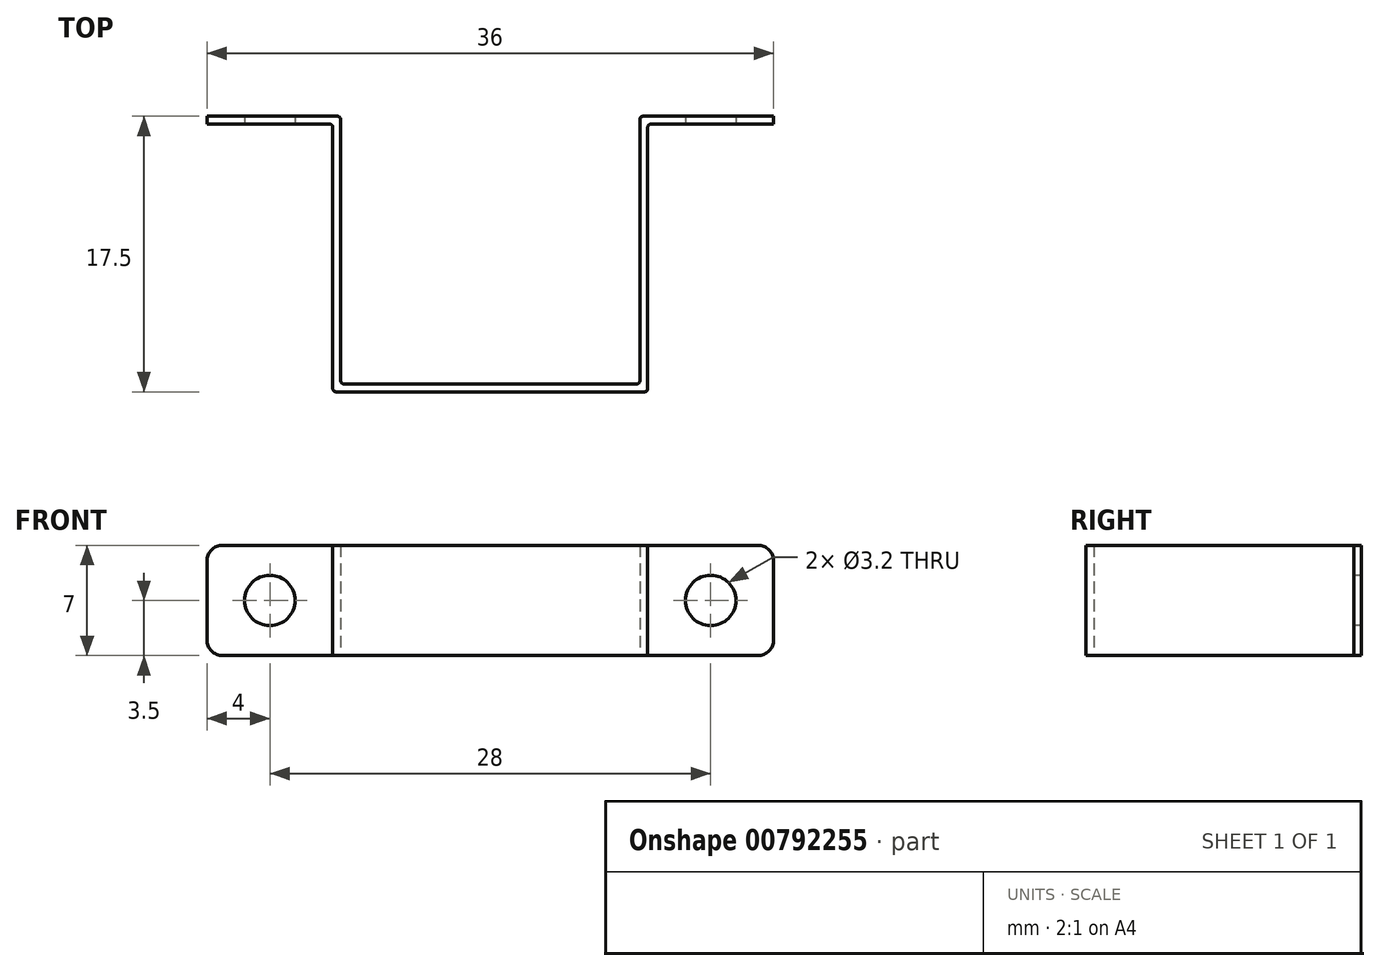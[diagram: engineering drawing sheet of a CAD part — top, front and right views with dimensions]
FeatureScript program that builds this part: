
annotation { "Feature Type Name" : "Feature", "Feature Type Description" : "" }
export const myFeature = defineFeature(function(context is Context, id is Id, definition is map)
    precondition{}
    {
        {
            var Q0;
            Q0=qCreatedBy(makeId("Top.planeOp"),FACE);
            var sketch = newSketch(context, id + "F0", { "sketchPlane" : qUnion([Q0])});
            skLineSegment(sketch, "E0", {"start": v(-10, 0) * mm, "end": v(10, 0) * mm});
            skLineSegment(sketch, "E1", {"start": v(-10, 0) * mm, "end": v(-10, 17) * mm});
            skLineSegment(sketch, "E2", {"start": v(-10, 17) * mm, "end": v(-18, 17) * mm});
            skLineSegment(sketch, "E3", {"start": v(10, 0) * mm, "end": v(10, 17) * mm});
            skLineSegment(sketch, "E4", {"start": v(10, 17) * mm, "end": v(18, 17) * mm});
            skLineSegment(sketch, "E5.0", {"start": v(9.5, 17.5) * mm, "end": v(18, 17.5) * mm});
            skLineSegment(sketch, "E5.1", {"start": v(-9.5, 17.5) * mm, "end": v(-18, 17.5) * mm});
            skLineSegment(sketch, "E5.2", {"start": v(-9.5, 0.5) * mm, "end": v(-9.5, 17.5) * mm});
            skLineSegment(sketch, "E5.3", {"start": v(-9.5, 0.5) * mm, "end": v(9.5, 0.5) * mm});
            skLineSegment(sketch, "E5.4", {"start": v(9.5, 0.5) * mm, "end": v(9.5, 17.5) * mm});
            skLineSegment(sketch, "E6", {"start": v(-18, 17.5) * mm, "end": v(-18, 17) * mm});
            skLineSegment(sketch, "E7", {"start": v(18, 17.5) * mm, "end": v(18, 17) * mm});
            skSolve(sketch);
        }
        {
            var Q0;
            Q0 = qSketchRegion(id + "F0", true);
            extrude(context, id + "F1", {"entities" : qUnion([Q0]), "depth" : 7 * mm, "offsetDistance" : 25 * mm});
        }
        {
            var Q0;
            Q0=makeQuery(id+"F1.opExtrude","SWEPT_EDGE",EDGE,{"disambiguationData":[OSD([sQuery(id+"F0.wireOp",EDGE,"E0"),sQuery(id+"F0.wireOp",EDGE,"E3")])]});
            var Q1;
            Q1=makeQuery(id+"F1.opExtrude","SWEPT_EDGE",EDGE,{"disambiguationData":[OSD([sQuery(id+"F0.wireOp",EDGE,"E0"),sQuery(id+"F0.wireOp",EDGE,"E1")])]});
            var Q2;
            Q2=makeQuery(id+"F1.opExtrude","SWEPT_EDGE",EDGE,{"disambiguationData":[OSD([sQuery(id+"F0.wireOp",EDGE,"E5.2"),sQuery(id+"F0.wireOp",EDGE,"E5.3")])]});
            var Q3;
            Q3=makeQuery(id+"F1.opExtrude","SWEPT_EDGE",EDGE,{"disambiguationData":[OSD([sQuery(id+"F0.wireOp",EDGE,"E5.3"),sQuery(id+"F0.wireOp",EDGE,"E5.4")])]});
            var Q4;
            Q4=makeQuery(id+"F1.opExtrude","SWEPT_EDGE",EDGE,{"disambiguationData":[OSD([sQuery(id+"F0.wireOp",EDGE,"E5.1"),sQuery(id+"F0.wireOp",EDGE,"E5.2")])]});
            var Q5;
            Q5=makeQuery(id+"F1.opExtrude","SWEPT_EDGE",EDGE,{"disambiguationData":[OSD([sQuery(id+"F0.wireOp",EDGE,"E1"),sQuery(id+"F0.wireOp",EDGE,"E2")])]});
            var Q6;
            Q6=makeQuery(id+"F1.opExtrude","SWEPT_EDGE",EDGE,{"disambiguationData":[OSD([sQuery(id+"F0.wireOp",EDGE,"E3"),sQuery(id+"F0.wireOp",EDGE,"E4")])]});
            var Q7;
            Q7=makeQuery(id+"F1.opExtrude","SWEPT_EDGE",EDGE,{"disambiguationData":[OSD([sQuery(id+"F0.wireOp",EDGE,"E5.0"),sQuery(id+"F0.wireOp",EDGE,"E5.4")])]});
            fillet(context, id + "F2", {"entities" : qUnion([Q0, Q1, Q2, Q3, Q4, Q5, Q6, Q7]), "radius" : 0.2 * mm, "tangentPropagation" : true, "allowEdgeOverflow" : false});
        }
        {
            var Q0;
            Q0=makeQuery(id+"F1.opExtrude","SWEPT_FACE",FACE,{"disambiguationData":[OSD([sQuery(id+"F0.wireOp",EDGE,"E4")])]});
            var sketch = newSketch(context, id + "F3", { "sketchPlane" : qUnion([Q0])});
            skCircle(sketch, "E8", {"center": v(14, 3.5) * mm, "radius": 1.6 * mm});
            skCircle(sketch, "E9", {"center": v(-14, 3.5) * mm, "radius": 1.6 * mm});
            skLineSegment(sketch, "E10", {"start": v(-14, 3.5) * mm, "end": v(14, 3.5) * mm, "construction": true});
            skSolve(sketch);
        }
        {
            var Q0;
            Q0 = qSketchRegion(id + "F3", true);
            extrude(context, id + "F4", {"entities" : qUnion([Q0]), "operationType" : NewBodyOperationType.REMOVE, "endBound" : BoundingType.THROUGH_ALL, "oppositeDirection" : true, "depth" : 25 * mm, "offsetDistance" : 25 * mm});
        }
        {
            var Q0;
            Q0=makeQuery(id+"F1.opExtrude","CAP_EDGE",EDGE,{"disambiguationData":[OSD([sQuery(id+"F0.wireOp",EDGE,"E7")])],"isStart":false});
            var Q1;
            Q1=makeQuery(id+"F1.opExtrude","CAP_EDGE",EDGE,{"disambiguationData":[OSD([sQuery(id+"F0.wireOp",EDGE,"E7")])],"isStart":true});
            var Q2;
            Q2=makeQuery(id+"F1.opExtrude","CAP_EDGE",EDGE,{"disambiguationData":[OSD([sQuery(id+"F0.wireOp",EDGE,"E6")])],"isStart":false});
            var Q3;
            Q3=makeQuery(id+"F1.opExtrude","CAP_EDGE",EDGE,{"disambiguationData":[OSD([sQuery(id+"F0.wireOp",EDGE,"E6")])],"isStart":true});
            fillet(context, id + "F5", {"entities" : qUnion([Q0, Q1, Q2, Q3]), "radius" : 1 * mm, "tangentPropagation" : true, "allowEdgeOverflow" : false});
        }
    });
